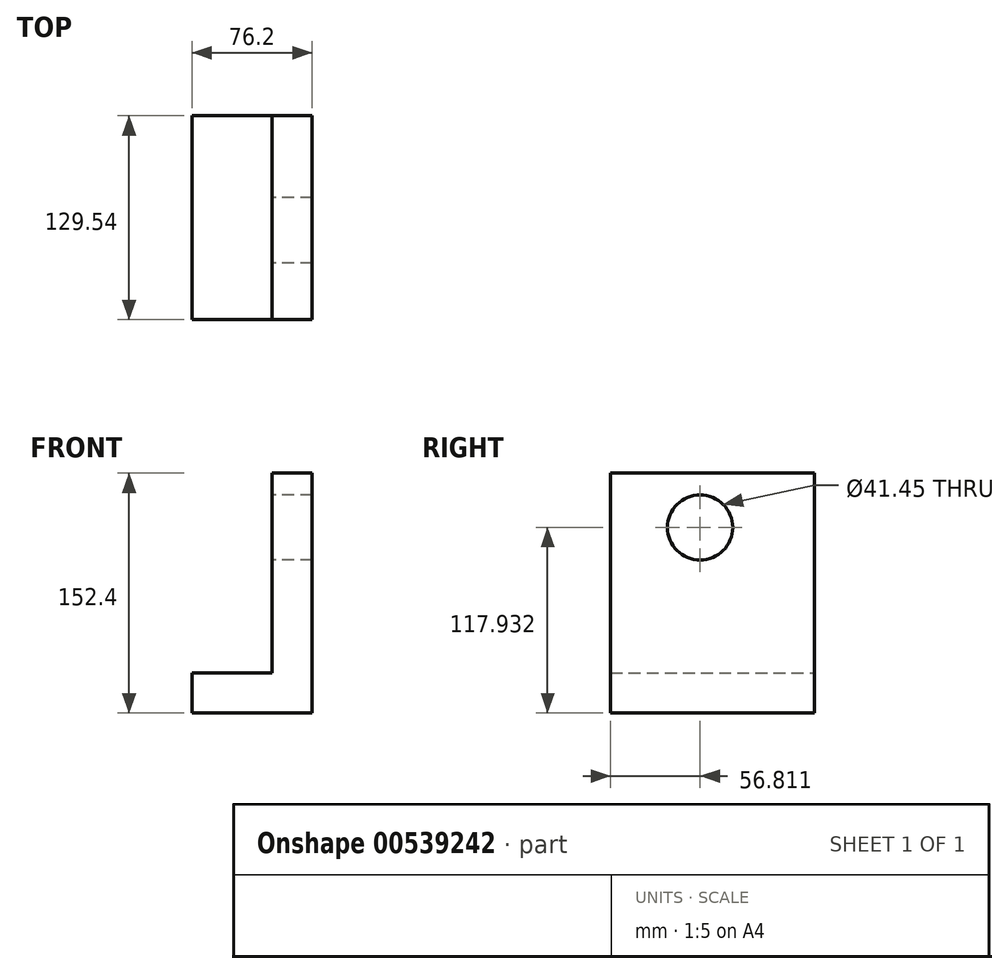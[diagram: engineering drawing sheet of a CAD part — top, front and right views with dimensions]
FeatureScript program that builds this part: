
annotation { "Feature Type Name" : "Feature", "Feature Type Description" : "" }
export const myFeature = defineFeature(function(context is Context, id is Id, definition is map)
    precondition{}
    {
        {
            var Q0;
            Q0=qCreatedBy(makeId("Front.planeOp"),FACE);
            var sketch = newSketch(context, id + "F0", { "sketchPlane" : qUnion([Q0])});
            skLineSegment(sketch, "E0", {"start": v(-76.2, 0) * mm, "end": v(-76.2, 25.4) * mm});
            skLineSegment(sketch, "E1", {"start": v(-76.2, 25.4) * mm, "end": v(-25.4, 25.4) * mm});
            skLineSegment(sketch, "E2", {"start": v(-25.4, 25.4) * mm, "end": v(-25.4, 152.4) * mm});
            skLineSegment(sketch, "E3", {"start": v(-25.4, 152.4) * mm, "end": v(0, 152.4) * mm});
            skLineSegment(sketch, "E4", {"start": v(-76.2, 0) * mm, "end": v(0, 0) * mm});
            skLineSegment(sketch, "E5", {"start": v(0, 152.4) * mm, "end": v(0, 0) * mm});
            skSolve(sketch);
        }
        {
            var Q0;
            Q0=makeQuery(id+"F0.imprint","IMPRINT",FACE,{"disambiguationData":[TD([[makeQuery(id+"F0.imprint","IMPRINT",EDGE,{"derivedFrom":sQuery(id+"F0.wireOp",EDGE,"E0")}),-1.0]])]});
            extrude(context, id + "F1", {"entities" : qUnion([Q0]), "endBound" : BoundingType.SYMMETRIC, "depth" : 25.4 * mm, "offsetDistance" : 25.4 * mm});
        }
        {
            var Q0;
            Q0=makeQuery(id+"F1.opExtrude","CAP_FACE",FACE,{"disambiguationData":[OSD([sQuery(id+"F0.wireOp",EDGE,"E0"),sQuery(id+"F0.wireOp",EDGE,"E1"),sQuery(id+"F0.wireOp",EDGE,"E2"),sQuery(id+"F0.wireOp",EDGE,"E3"),sQuery(id+"F0.wireOp",EDGE,"E4"),sQuery(id+"F0.wireOp",EDGE,"E5")])],"isStart":false});
            extrude(context, id + "F2", {"entities" : qUnion([Q0]), "operationType" : NewBodyOperationType.ADD, "oppositeDirection" : true, "depth" : 129.54 * mm, "offsetDistance" : 25.4 * mm});
        }
        {
            var Q0;
            {var subQ0=sQuery(id+"F0.wireOp",EDGE,"E2");Q0=makeQuery(id+"F2.boolean.opBoolean","MERGE",FACE,{"derivedFrom":[makeQuery(id+"F1.opExtrude","SWEPT_FACE",FACE,{"disambiguationData":[OSD([subQ0])]}),makeQuery(id+"F2.opExtrude","SWEPT_FACE",FACE,{"disambiguationData":[OSD([subQ0])]})]});}
            var sketch = newSketch(context, id + "F3", { "sketchPlane" : qUnion([Q0])});
            skCircle(sketch, "E6", {"center": v(-44.11, 117.93) * mm, "radius": 20.73 * mm});
            skSolve(sketch);
        }
        {
            var Q0;
            Q0=makeQuery(id+"F3.imprint","IMPRINT",FACE,{"disambiguationData":[TD([[makeQuery(id+"F3.imprint","IMPRINT",EDGE,{"derivedFrom":sQuery(id+"F3.wireOp",EDGE,"E6")}),1.0]])]});
            extrude(context, id + "F4", {"entities" : qUnion([Q0]), "operationType" : NewBodyOperationType.REMOVE, "endBound" : BoundingType.SYMMETRIC, "oppositeDirection" : true, "depth" : 434.85 * mm, "offsetDistance" : 25.4 * mm});
        }
    });
